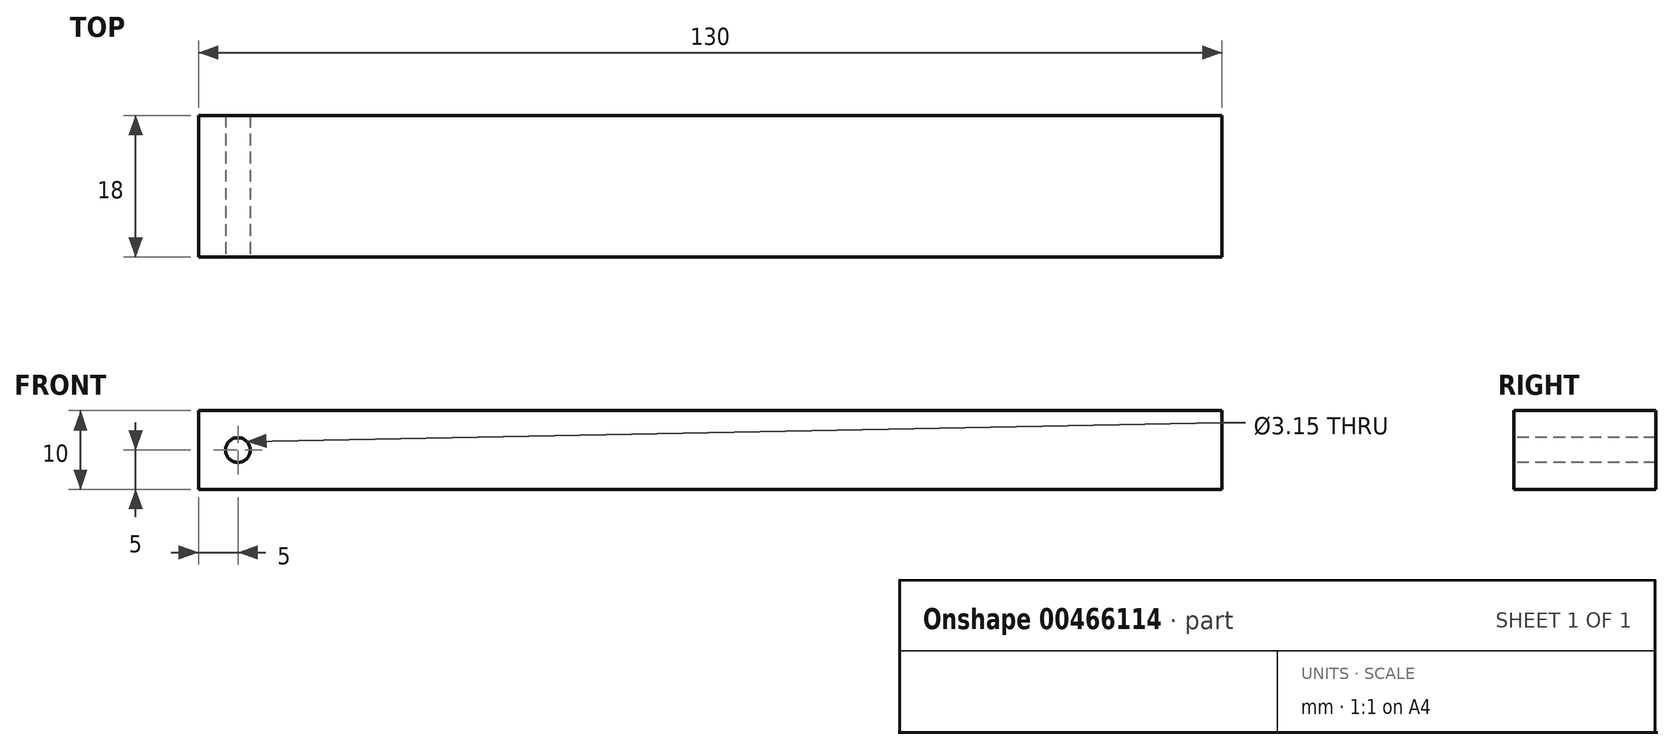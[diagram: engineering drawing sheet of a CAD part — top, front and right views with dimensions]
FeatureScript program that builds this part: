
annotation { "Feature Type Name" : "Feature", "Feature Type Description" : "" }
export const myFeature = defineFeature(function(context is Context, id is Id, definition is map)
    precondition{}
    {
        {
            var Q0;
            Q0=qCreatedBy(makeId("Top.planeOp"),FACE);
            var sketch = newSketch(context, id + "F0", { "sketchPlane" : qUnion([Q0])});
            skLineSegment(sketch, "E0", {"start": v(0, 18) * mm, "end": v(0, 0) * mm});
            skLineSegment(sketch, "E1", {"start": v(0, 0) * mm, "end": v(130, 0) * mm});
            skLineSegment(sketch, "E2", {"start": v(130, 0) * mm, "end": v(130, 18) * mm});
            skLineSegment(sketch, "E3", {"start": v(130, 18) * mm, "end": v(0, 18) * mm});
            skSolve(sketch);
        }
        {
            var Q0;
            Q0=makeQuery(id+"F0.imprint","IMPRINT",FACE,{"disambiguationData":[TD([[makeQuery(id+"F0.imprint","IMPRINT",EDGE,{"derivedFrom":sQuery(id+"F0.wireOp",EDGE,"E0")}),1.0]])]});
            extrude(context, id + "F1", {"entities" : qUnion([Q0]), "depth" : 10 * mm});
        }
        {
            var Q0;
            Q0=makeQuery(id+"F1.opExtrude","SWEPT_FACE",FACE,{"disambiguationData":[OSD([sQuery(id+"F0.wireOp",EDGE,"E1")])]});
            var sketch = newSketch(context, id + "F2", { "sketchPlane" : qUnion([Q0])});
            skLineSegment(sketch, "E4", {"start": v(0, 5) * mm, "end": v(5, 5) * mm, "construction": true});
            skLineSegment(sketch, "E5", {"start": v(5, 5) * mm, "end": v(5, 0) * mm, "construction": true});
            skSolve(sketch);
        }
        {
            var Q0;
            Q0=sQuery(id+"F2.wireOp",VERTEX,"E5.start");
            var Q1;
            Q1=makeQuery(id+"F1.opExtrude","SWEPT_BODY",BODY,{"disambiguationData":[OSD([sQuery(id+"F0.wireOp",EDGE,"E0"),sQuery(id+"F0.wireOp",EDGE,"E1"),sQuery(id+"F0.wireOp",EDGE,"E2"),sQuery(id+"F0.wireOp",EDGE,"E3")])]});
            hole(context, id + "F3", {"style" : HoleStyle.SIMPLE, "endStyle" : HoleEndStyle.THROUGH, "standardTappedOrClearance" : lookupTablePath({ "standard" : "ISO", "fit" : "Close", "size" : "M3", "type" : "Clearance" }), "standardBlindInLast" : lookupTablePath({ "fit" : "Close", "standard" : "ISO", "size" : "M3", "type" : "Clearance" }), "holeDiameter" : 3.15 * mm, "isTappedThrough" : true, "tappedDepth" : 12 * mm, "tapClearance" : 3, "locations" : qUnion([Q0]), "scope" : qUnion([Q1])});
        }
    });
